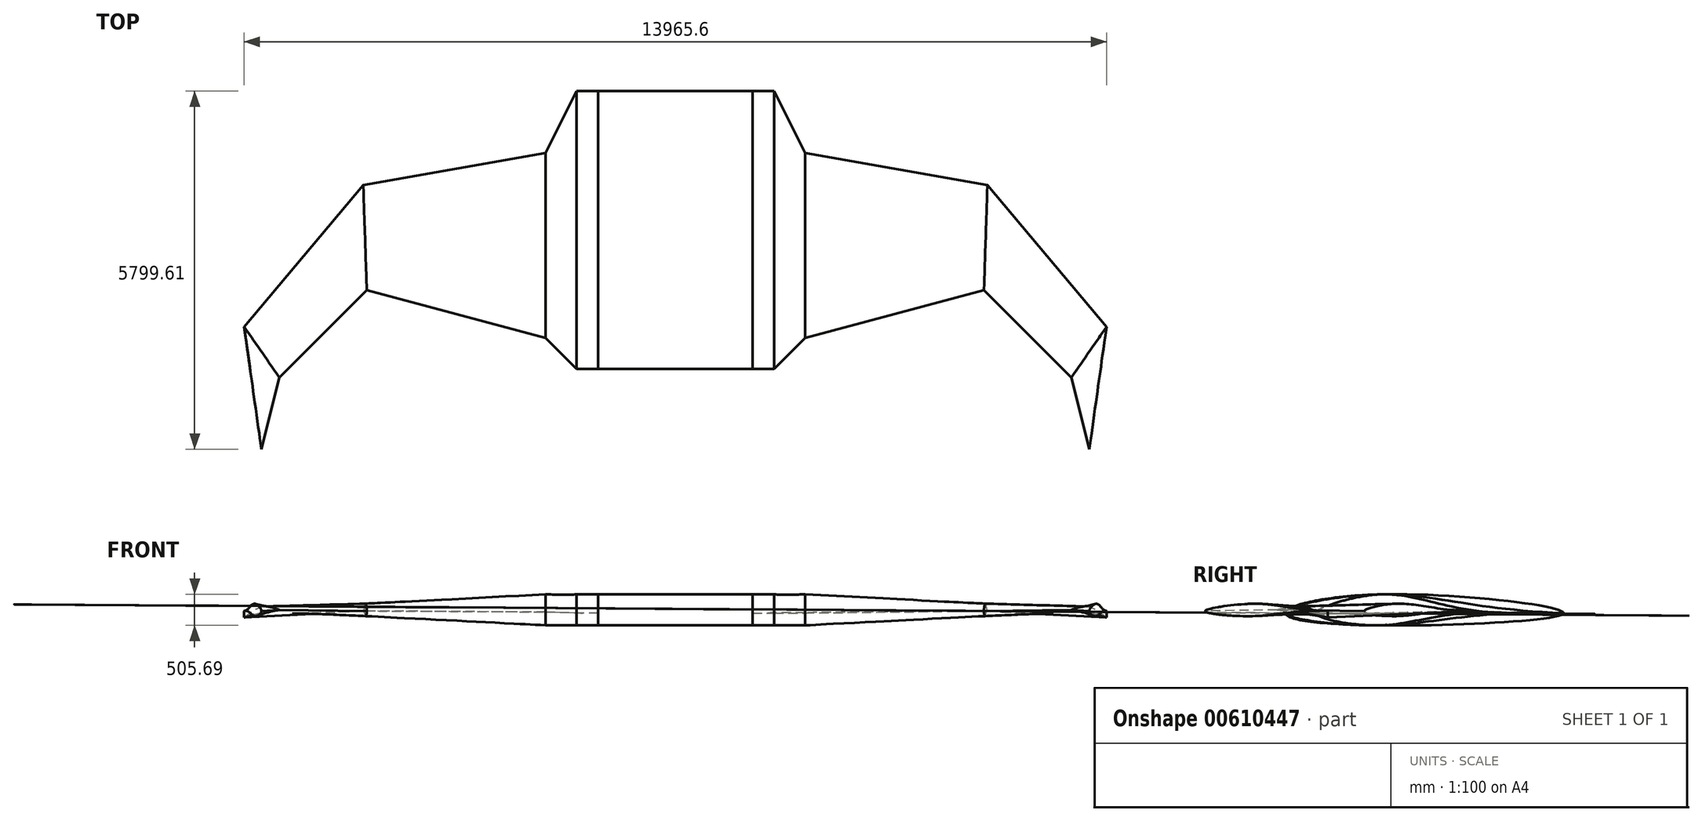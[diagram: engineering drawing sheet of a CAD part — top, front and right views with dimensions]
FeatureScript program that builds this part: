
annotation { "Feature Type Name" : "Feature", "Feature Type Description" : "" }
export const myFeature = defineFeature(function(context is Context, id is Id, definition is map)
    precondition{}
    {
        {
            var Q0;
            Q0=qCreatedBy(makeId("Top.planeOp"),FACE);
            var sketch = newSketch(context, id + "F0", { "sketchPlane" : qUnion([Q0])});
            skLineSegment(sketch, "E0", {"start": v(0, 0) * mm, "end": v(-1250, 0) * mm});
            skLineSegment(sketch, "E1", {"start": v(-1250, 0) * mm, "end": v(-1600, 0) * mm});
            skLineSegment(sketch, "E2", {"start": v(-1600, 0) * mm, "end": v(-2100, 0) * mm});
            skLineSegment(sketch, "E3", {"start": v(-1600, 0) * mm, "end": v(-1600, -1500) * mm});
            skLineSegment(sketch, "E4", {"start": v(-1600, 0) * mm, "end": v(-1600, 3000) * mm});
            skLineSegment(sketch, "E5", {"start": v(-2100, 0) * mm, "end": v(-2100, -1000) * mm});
            skLineSegment(sketch, "E6", {"start": v(-2100, 0) * mm, "end": v(-2100, 2000) * mm});
            skLineSegment(sketch, "E7", {"start": v(-2100, -1000) * mm, "end": v(-4997.78, -223.54) * mm});
            skLineSegment(sketch, "E8", {"start": v(-2100, 2000) * mm, "end": v(-5054.42, 1479.06) * mm});
            skLineSegment(sketch, "E9", {"start": v(-4997.78, -223.54) * mm, "end": v(-5054.42, 1479.06) * mm});
            skLineSegment(sketch, "E10", {"start": v(-4997.78, -223.54) * mm, "end": v(-6412, -1637.76) * mm});
            skLineSegment(sketch, "E11", {"start": v(-5054.42, 1479.06) * mm, "end": v(-6982.79, -819.08) * mm});
            skLineSegment(sketch, "E12", {"start": v(-6412, -1637.76) * mm, "end": v(-6982.79, -819.08) * mm});
            skLineSegment(sketch, "E13", {"start": v(-6412, -1637.76) * mm, "end": v(-6704.44, -2799.61) * mm});
            skLineSegment(sketch, "E14", {"start": v(-6704.44, -2799.61) * mm, "end": v(-6982.79, -819.08) * mm});
            skLineSegment(sketch, "E15", {"start": v(0, 0) * mm, "end": v(1250, 0) * mm});
            skLineSegment(sketch, "E16", {"start": v(1250, 0) * mm, "end": v(1600, 0) * mm});
            skLineSegment(sketch, "E17", {"start": v(1600, 0) * mm, "end": v(2100, 0) * mm});
            skLineSegment(sketch, "E18", {"start": v(1600, 0) * mm, "end": v(1600, -1500) * mm});
            skLineSegment(sketch, "E19", {"start": v(1600, 0) * mm, "end": v(1600, 3000) * mm});
            skLineSegment(sketch, "E20", {"start": v(2100, 0) * mm, "end": v(2100, -1000) * mm});
            skLineSegment(sketch, "E21", {"start": v(2100, 0) * mm, "end": v(2100, 2000) * mm});
            skLineSegment(sketch, "E22", {"start": v(2100, -1000) * mm, "end": v(4997.78, -223.54) * mm});
            skLineSegment(sketch, "E23", {"start": v(2100, 2000) * mm, "end": v(5054.42, 1479.06) * mm});
            skLineSegment(sketch, "E24", {"start": v(4997.78, -223.54) * mm, "end": v(5054.42, 1479.06) * mm});
            skLineSegment(sketch, "E25", {"start": v(4997.78, -223.54) * mm, "end": v(6412, -1637.76) * mm});
            skLineSegment(sketch, "E26", {"start": v(5054.42, 1479.06) * mm, "end": v(6982.79, -819.08) * mm});
            skLineSegment(sketch, "E27", {"start": v(6412, -1637.76) * mm, "end": v(6982.79, -819.08) * mm});
            skLineSegment(sketch, "E28", {"start": v(6412, -1637.76) * mm, "end": v(6704.44, -2799.61) * mm});
            skLineSegment(sketch, "E29", {"start": v(6704.44, -2799.61) * mm, "end": v(6982.79, -819.08) * mm});
            skSolve(sketch);
        }
        {
            var Q0;
            Q0=qCreatedBy(makeId("Right.planeOp"),FACE);
            var sketch = newSketch(context, id + "F1", { "sketchPlane" : qUnion([Q0])});
            skFitSpline(sketch, "E30", {"points": [v(-1500, -50) * mm, v(0, 250) * mm, v(3000, -50) * mm], "startDerivative": vector(0, 887.04) * mm, "endDerivative": vector(0, -631.84) * mm});
            skFitSpline(sketch, "E31", {"points": [v(-1500, -50) * mm, v(0, -250) * mm, v(3000, -50) * mm], "startDerivative": vector(0, -903.58) * mm, "endDerivative": vector(0, 641.04) * mm});
            skSolve(sketch);
        }
        {
            var Q0;
            Q0=qCreatedBy(makeId("Right.planeOp"),FACE);
            cPlane(context, id + "F2", {"entities" : qUnion([Q0]), "cplaneType" : CPlaneType.OFFSET, "offset" : 1600 * mm, "oppositeDirection" : true, "width" : 150 * mm, "height" : 150 * mm});
        }
        {
            var Q0;
            Q0=qCreatedBy(id+"F2.planeOp",FACE);
            var sketch = newSketch(context, id + "F3", { "sketchPlane" : qUnion([Q0])});
            skFitSpline(sketch, "E32", {"points": [v(-1500, -50) * mm, v(0, 250) * mm, v(3000, -50) * mm], "startDerivative": vector(0, 887.04) * mm, "endDerivative": vector(7705.35, -256.85) * mm});
            skFitSpline(sketch, "E33", {"points": [v(-1500, -50) * mm, v(0, -250) * mm, v(3000, -50) * mm], "startDerivative": vector(0, -722.87) * mm, "endDerivative": vector(7692.49, -256.42) * mm});
            skSolve(sketch);
        }
        {
            var Q0;
            Q0=qCreatedBy(makeId("Right.planeOp"),FACE);
            cPlane(context, id + "F4", {"entities" : qUnion([Q0]), "cplaneType" : CPlaneType.OFFSET, "offset" : 1600 * mm, "width" : 150 * mm, "height" : 150 * mm});
        }
        {
            var Q0;
            Q0=qCreatedBy(id+"F4.planeOp",FACE);
            var sketch = newSketch(context, id + "F5", { "sketchPlane" : qUnion([Q0])});
            skFitSpline(sketch, "E34", {"points": [v(-1500, -50) * mm, v(0, 250) * mm, v(3000, -50) * mm], "startDerivative": vector(0, 887.04) * mm, "endDerivative": vector(7705.35, -256.85) * mm});
            skFitSpline(sketch, "E35", {"points": [v(-1500, -50) * mm, v(0, -250) * mm, v(3000, -50) * mm], "startDerivative": vector(0, -722.87) * mm, "endDerivative": vector(7692.49, -256.42) * mm});
            skSolve(sketch);
        }
        {
            var Q0;
            Q0=qCreatedBy(makeId("Right.planeOp"),FACE);
            cPlane(context, id + "F6", {"entities" : qUnion([Q0]), "cplaneType" : CPlaneType.OFFSET, "offset" : 2100 * mm, "oppositeDirection" : true, "width" : 150 * mm, "height" : 150 * mm});
        }
        {
            var Q0;
            Q0=qCreatedBy(id+"F6.planeOp",FACE);
            var sketch = newSketch(context, id + "F7", { "sketchPlane" : qUnion([Q0])});
            skFitSpline(sketch, "E36", {"points": [v(-1000, -36) * mm, v(0, 250) * mm, v(2000, -36) * mm], "startDerivative": vector(0, 574.5) * mm, "endDerivative": vector(5152.5, -185.5) * mm});
            skFitSpline(sketch, "E37", {"points": [v(-1000, -36) * mm, v(0, -250) * mm, v(2000, -36) * mm], "startDerivative": vector(0, -699.11) * mm, "endDerivative": vector(5139.1, -185) * mm});
            skSolve(sketch);
        }
        {
            var Q0;
            Q0=qCreatedBy(makeId("Right.planeOp"),FACE);
            cPlane(context, id + "F8", {"entities" : qUnion([Q0]), "cplaneType" : CPlaneType.OFFSET, "offset" : 2100 * mm, "width" : 150 * mm, "height" : 150 * mm});
        }
        {
            var Q0;
            Q0=qCreatedBy(id+"F8.planeOp",FACE);
            var sketch = newSketch(context, id + "F9", { "sketchPlane" : qUnion([Q0])});
            skFitSpline(sketch, "E38", {"points": [v(-1000, -50) * mm, v(0, 250) * mm, v(2000, -50) * mm], "startDerivative": vector(0, 574.03) * mm, "endDerivative": vector(5155.5, -257.77) * mm});
            skFitSpline(sketch, "E39", {"points": [v(-1000, -50) * mm, v(0, -250) * mm, v(2000, -50) * mm], "startDerivative": vector(0, -699.54) * mm, "endDerivative": vector(5136.9, -256.85) * mm});
            skSolve(sketch);
        }
        {
            var Q0;
            Q0=sQuery(id+"F0.wireOp",EDGE,"E9");
            cPlane(context, id + "F10", {"entities" : qUnion([Q0]), "cplaneType" : CPlaneType.LINE_ANGLE, "offset" : 25 * mm, "angle" : 90 * degree, "oppositeDirection" : true, "width" : 150 * mm, "height" : 150 * mm});
        }
        {
            var Q0;
            Q0=qCreatedBy(id+"F10.planeOp",FACE);
            var sketch = newSketch(context, id + "F11", { "sketchPlane" : qUnion([Q0])});
            skFitSpline(sketch, "E40", {"points": [v(57.23, -18) * mm, v(-442.77, 100) * mm, v(-1646.3, -18) * mm], "startDerivative": vector(0, 311.71) * mm, "endDerivative": vector(-2981.97, -89.2) * mm});
            skFitSpline(sketch, "E41", {"points": [v(57.23, -18) * mm, v(-442.77, -100) * mm, v(-1646.3, -18) * mm], "startDerivative": vector(0, -370) * mm, "endDerivative": vector(-2975.3, -89) * mm});
            skSolve(sketch);
        }
        {
            var Q0;
            Q0=sQuery(id+"F0.wireOp",EDGE,"E24");
            cPlane(context, id + "F12", {"entities" : qUnion([Q0]), "cplaneType" : CPlaneType.LINE_ANGLE, "offset" : 25 * mm, "angle" : 90 * degree, "width" : 150 * mm, "height" : 150 * mm});
        }
        {
            var Q0;
            Q0=qCreatedBy(id+"F12.planeOp",FACE);
            var sketch = newSketch(context, id + "F13", { "sketchPlane" : qUnion([Q0])});
            skFitSpline(sketch, "E42", {"points": [v(-57.23, -18) * mm, v(442.77, 100) * mm, v(1646.3, -18) * mm], "startDerivative": vector(0, 311.71) * mm, "endDerivative": vector(2981.97, -89.2) * mm});
            skFitSpline(sketch, "E43", {"points": [v(-57.23, -18) * mm, v(442.77, -100) * mm, v(1646.3, -18) * mm], "startDerivative": vector(0, -370) * mm, "endDerivative": vector(2975.3, -89) * mm});
            skSolve(sketch);
        }
        {
            var Q0;
            Q0=sQuery(id+"F0.wireOp",EDGE,"E12");
            cPlane(context, id + "F14", {"entities" : qUnion([Q0]), "cplaneType" : CPlaneType.LINE_ANGLE, "offset" : 25 * mm, "angle" : 90 * degree, "oppositeDirection" : true, "width" : 150 * mm, "height" : 150 * mm});
        }
        {
            var Q0;
            Q0=qCreatedBy(id+"F14.planeOp",FACE);
            var sketch = newSketch(context, id + "F15", { "sketchPlane" : qUnion([Q0])});
            skFitSpline(sketch, "E44", {"points": [v(-2323.74, 0) * mm, v(-2822.75, 50) * mm, v(-3321.76, -125) * mm], "startDerivative": vector(-1017.94, 211.55) * mm, "endDerivative": vector(-978.27, -458.6) * mm});
            skFitSpline(sketch, "E45", {"points": [v(-2323.74, 0) * mm, v(-2822.75, -50) * mm, v(-3321.76, -125) * mm], "startDerivative": vector(-1000.33, -87.77) * mm, "endDerivative": vector(-995.7, -162.2) * mm});
            skSolve(sketch);
        }
        {
            var Q0;
            Q0=sQuery(id+"F0.wireOp",EDGE,"E27");
            cPlane(context, id + "F16", {"entities" : qUnion([Q0]), "cplaneType" : CPlaneType.LINE_ANGLE, "offset" : 25 * mm, "angle" : 90 * degree, "width" : 150 * mm, "height" : 150 * mm});
        }
        {
            var Q0;
            Q0=qCreatedBy(id+"F16.planeOp",FACE);
            var sketch = newSketch(context, id + "F17", { "sketchPlane" : qUnion([Q0])});
            skFitSpline(sketch, "E46", {"points": [v(2323.74, 0) * mm, v(2822.75, 50) * mm, v(3321.76, -125) * mm], "startDerivative": vector(1017.94, 211.55) * mm, "endDerivative": vector(978.27, -458.6) * mm});
            skFitSpline(sketch, "E47", {"points": [v(2323.74, 0) * mm, v(2822.75, -50) * mm, v(3321.76, -125) * mm], "startDerivative": vector(1000.33, -87.77) * mm, "endDerivative": vector(995.7, -162.2) * mm});
            skSolve(sketch);
        }
        {
            var Q0;
            Q0=sQuery(id+"F0.wireOp",EDGE,"E14");
            cPlane(context, id + "F18", {"entities" : qUnion([Q0]), "cplaneType" : CPlaneType.LINE_ANGLE, "offset" : 25 * mm, "angle" : 90 * degree, "oppositeDirection" : true, "width" : 150 * mm, "height" : 150 * mm});
        }
        {
            var Q0;
            Q0=qCreatedBy(id+"F18.planeOp",FACE);
            var sketch = newSketch(context, id + "F19", { "sketchPlane" : qUnion([Q0])});
            skFitSpline(sketch, "E48", {"points": [v(1839.3, -18) * mm, v(1039.3, 100) * mm, v(-160.7, -18) * mm], "startDerivative": vector(0, 273.2) * mm, "endDerivative": vector(-3274.07, -98.22) * mm});
            skFitSpline(sketch, "E49", {"points": [v(1839.3, -18) * mm, v(1039.3, -100) * mm, v(-160.7, -18) * mm], "startDerivative": vector(0, -323.44) * mm, "endDerivative": vector(-3271.82, -98.15) * mm});
            skSolve(sketch);
        }
        {
            var Q0;
            Q0=sQuery(id+"F0.wireOp",EDGE,"E29");
            cPlane(context, id + "F20", {"entities" : qUnion([Q0]), "cplaneType" : CPlaneType.LINE_ANGLE, "offset" : 25 * mm, "angle" : 90 * degree, "width" : 150 * mm, "height" : 150 * mm});
        }
        {
            var Q0;
            Q0=qCreatedBy(id+"F20.planeOp",FACE);
            var sketch = newSketch(context, id + "F21", { "sketchPlane" : qUnion([Q0])});
            skFitSpline(sketch, "E50", {"points": [v(-1839.3, -18) * mm, v(-1039.3, 100) * mm, v(160.7, -18) * mm], "startDerivative": vector(0, 273.2) * mm, "endDerivative": vector(3274.07, -98.22) * mm});
            skFitSpline(sketch, "E51", {"points": [v(-1839.3, -18) * mm, v(-1039.3, -100) * mm, v(160.7, -18) * mm], "startDerivative": vector(0, -323.44) * mm, "endDerivative": vector(3271.82, -98.15) * mm});
            skSolve(sketch);
        }
        {
            var Q0;
            Q0=makeQuery(id+"F1.imprint","IMPRINT",FACE,{"disambiguationData":[TD([[makeQuery(id+"F1.imprint","IMPRINT",EDGE,{"derivedFrom":sQuery(id+"F1.wireOp",EDGE,"E30")}),-1.0]])]});
            extrude(context, id + "F22", {"entities" : qUnion([Q0]), "endBound" : BoundingType.SYMMETRIC, "depth" : 2500 * mm, "offsetDistance" : 25 * mm});
        }
        {
            var Q1;
            Q1=makeQuery(id+"F22.opExtrude","CAP_FACE",FACE,{"disambiguationData":[OSD([sQuery(id+"F1.wireOp",EDGE,"E30"),sQuery(id+"F1.wireOp",EDGE,"E31")])],"isStart":true});
            var Q2;
            {var subQ0=sQuery(id+"F3.wireOp",EDGE,"E32");Q2=makeQuery(id+"F3.imprint","IMPRINT",FACE,{"disambiguationData":[TD([[makeQuery(id+"F3.imprint","IMPRINT",EDGE,{"derivedFrom":subQ0}),-1.0]])]});}
            loft(context, id + "F23", {"operationType" : NewBodyOperationType.ADD, "sheetProfilesArray" : [{ "sheetProfileEntities" : qUnion([Q1]) }, { "sheetProfileEntities" : qUnion([Q2]) }]});
        }
        {
            var Q1;
            Q1=makeQuery(id+"F22.opExtrude","CAP_FACE",FACE,{"disambiguationData":[OSD([sQuery(id+"F1.wireOp",EDGE,"E30"),sQuery(id+"F1.wireOp",EDGE,"E31")])],"isStart":false});
            var Q2;
            {var subQ0=sQuery(id+"F5.wireOp",EDGE,"E34");Q2=makeQuery(id+"F5.imprint","IMPRINT",FACE,{"disambiguationData":[TD([[makeQuery(id+"F5.imprint","IMPRINT",EDGE,{"derivedFrom":subQ0}),-1.0]])]});}
            loft(context, id + "F24", {"operationType" : NewBodyOperationType.ADD, "sheetProfilesArray" : [{ "sheetProfileEntities" : qUnion([Q1]) }, { "sheetProfileEntities" : qUnion([Q2]) }]});
        }
        {
            var Q1;
            {var subQ0=sQuery(id+"F3.wireOp",EDGE,"E32");Q1=makeQuery(id+"F23.opLoft","CAP_FACE",FACE,{"disambiguationData":[OSD([makeQuery(id+"F3.imprint","IMPRINT",FACE,{"disambiguationData":[TD([[makeQuery(id+"F3.imprint","IMPRINT",EDGE,{"derivedFrom":subQ0}),-1.0]])]})])],"isStart":true});}
            var Q2;
            {var subQ0=sQuery(id+"F7.wireOp",EDGE,"E36");Q2=makeQuery(id+"F7.imprint","IMPRINT",FACE,{"disambiguationData":[TD([[makeQuery(id+"F7.imprint","IMPRINT",EDGE,{"derivedFrom":subQ0}),-1.0]])]});}
            loft(context, id + "F25", {"operationType" : NewBodyOperationType.ADD, "sheetProfilesArray" : [{ "sheetProfileEntities" : qUnion([Q1]) }, { "sheetProfileEntities" : qUnion([Q2]) }]});
        }
        {
            var Q1;
            {var subQ0=sQuery(id+"F5.wireOp",EDGE,"E34");Q1=makeQuery(id+"F24.opLoft","CAP_FACE",FACE,{"disambiguationData":[OSD([makeQuery(id+"F5.imprint","IMPRINT",FACE,{"disambiguationData":[TD([[makeQuery(id+"F5.imprint","IMPRINT",EDGE,{"derivedFrom":subQ0}),-1.0]])]})])],"isStart":true});}
            var Q2;
            {var subQ0=sQuery(id+"F9.wireOp",EDGE,"E38");Q2=makeQuery(id+"F9.imprint","IMPRINT",FACE,{"disambiguationData":[TD([[makeQuery(id+"F9.imprint","IMPRINT",EDGE,{"derivedFrom":subQ0}),-1.0]])]});}
            loft(context, id + "F26", {"operationType" : NewBodyOperationType.ADD, "sheetProfilesArray" : [{ "sheetProfileEntities" : qUnion([Q1]) }, { "sheetProfileEntities" : qUnion([Q2]) }]});
        }
        {
            var Q1;
            {var subQ0=sQuery(id+"F7.wireOp",EDGE,"E36");Q1=makeQuery(id+"F25.opLoft","CAP_FACE",FACE,{"disambiguationData":[OSD([makeQuery(id+"F7.imprint","IMPRINT",FACE,{"disambiguationData":[TD([[makeQuery(id+"F7.imprint","IMPRINT",EDGE,{"derivedFrom":subQ0}),-1.0]])]})])],"isStart":true});}
            var Q2;
            {var subQ0=sQuery(id+"F11.wireOp",EDGE,"E40");Q2=makeQuery(id+"F11.imprint","IMPRINT",FACE,{"disambiguationData":[TD([[makeQuery(id+"F11.imprint","IMPRINT",EDGE,{"derivedFrom":subQ0}),1.0]])]});}
            loft(context, id + "F27", {"operationType" : NewBodyOperationType.ADD, "sheetProfilesArray" : [{ "sheetProfileEntities" : qUnion([Q1]) }, { "sheetProfileEntities" : qUnion([Q2]) }]});
        }
        {
            var Q1;
            {var subQ0=sQuery(id+"F9.wireOp",EDGE,"E38");Q1=makeQuery(id+"F26.opLoft","CAP_FACE",FACE,{"disambiguationData":[OSD([makeQuery(id+"F9.imprint","IMPRINT",FACE,{"disambiguationData":[TD([[makeQuery(id+"F9.imprint","IMPRINT",EDGE,{"derivedFrom":subQ0}),-1.0]])]})])],"isStart":true});}
            var Q2;
            {var subQ0=sQuery(id+"F13.wireOp",EDGE,"E42");Q2=makeQuery(id+"F13.imprint","IMPRINT",FACE,{"disambiguationData":[TD([[makeQuery(id+"F13.imprint","IMPRINT",EDGE,{"derivedFrom":subQ0}),-1.0]])]});}
            loft(context, id + "F28", {"operationType" : NewBodyOperationType.ADD, "sheetProfilesArray" : [{ "sheetProfileEntities" : qUnion([Q1]) }, { "sheetProfileEntities" : qUnion([Q2]) }]});
        }
        {
            var Q1;
            {var subQ0=sQuery(id+"F11.wireOp",EDGE,"E40");Q1=makeQuery(id+"F27.opLoft","CAP_FACE",FACE,{"disambiguationData":[OSD([makeQuery(id+"F11.imprint","IMPRINT",FACE,{"disambiguationData":[TD([[makeQuery(id+"F11.imprint","IMPRINT",EDGE,{"derivedFrom":subQ0}),1.0]])]})])],"isStart":true});}
            var Q2;
            Q2=makeQuery(id+"F15.imprint","IMPRINT",FACE,{"disambiguationData":[TD([[makeQuery(id+"F15.imprint","IMPRINT",EDGE,{"derivedFrom":sQuery(id+"F15.wireOp",EDGE,"E44")}),1.0]])]});
            loft(context, id + "F29", {"operationType" : NewBodyOperationType.ADD, "sheetProfilesArray" : [{ "sheetProfileEntities" : qUnion([Q1]) }, { "sheetProfileEntities" : qUnion([Q2]) }]});
        }
        {
            var Q1;
            {var subQ0=sQuery(id+"F13.wireOp",EDGE,"E42");Q1=makeQuery(id+"F28.opLoft","CAP_FACE",FACE,{"disambiguationData":[OSD([makeQuery(id+"F13.imprint","IMPRINT",FACE,{"disambiguationData":[TD([[makeQuery(id+"F13.imprint","IMPRINT",EDGE,{"derivedFrom":subQ0}),-1.0]])]})])],"isStart":true});}
            var Q2;
            Q2=makeQuery(id+"F17.imprint","IMPRINT",FACE,{"disambiguationData":[TD([[makeQuery(id+"F17.imprint","IMPRINT",EDGE,{"derivedFrom":sQuery(id+"F17.wireOp",EDGE,"E46")}),-1.0]])]});
            loft(context, id + "F30", {"operationType" : NewBodyOperationType.ADD, "sheetProfilesArray" : [{ "sheetProfileEntities" : qUnion([Q1]) }, { "sheetProfileEntities" : qUnion([Q2]) }]});
        }
        {
            var Q1;
            Q1=makeQuery(id+"F29.opLoft","CAP_FACE",FACE,{"disambiguationData":[OSD([makeQuery(id+"F15.imprint","IMPRINT",FACE,{"disambiguationData":[TD([[makeQuery(id+"F15.imprint","IMPRINT",EDGE,{"derivedFrom":sQuery(id+"F15.wireOp",EDGE,"E44")}),1.0]])]})])],"isStart":true});
            var Q2;
            {var subQ0=sQuery(id+"F19.wireOp",EDGE,"E48");Q2=makeQuery(id+"F19.imprint","IMPRINT",FACE,{"disambiguationData":[TD([[makeQuery(id+"F19.imprint","IMPRINT",EDGE,{"derivedFrom":subQ0}),1.0]])]});}
            loft(context, id + "F31", {"operationType" : NewBodyOperationType.ADD, "sheetProfilesArray" : [{ "sheetProfileEntities" : qUnion([Q1]) }, { "sheetProfileEntities" : qUnion([Q2]) }]});
        }
        {
            var Q1;
            Q1=makeQuery(id+"F30.opLoft","CAP_FACE",FACE,{"disambiguationData":[OSD([makeQuery(id+"F17.imprint","IMPRINT",FACE,{"disambiguationData":[TD([[makeQuery(id+"F17.imprint","IMPRINT",EDGE,{"derivedFrom":sQuery(id+"F17.wireOp",EDGE,"E46")}),-1.0]])]})])],"isStart":true});
            var Q2;
            {var subQ0=sQuery(id+"F21.wireOp",EDGE,"E50");Q2=makeQuery(id+"F21.imprint","IMPRINT",FACE,{"disambiguationData":[TD([[makeQuery(id+"F21.imprint","IMPRINT",EDGE,{"derivedFrom":subQ0}),-1.0]])]});}
            loft(context, id + "F32", {"operationType" : NewBodyOperationType.ADD, "sheetProfilesArray" : [{ "sheetProfileEntities" : qUnion([Q1]) }, { "sheetProfileEntities" : qUnion([Q2]) }]});
        }
    });
